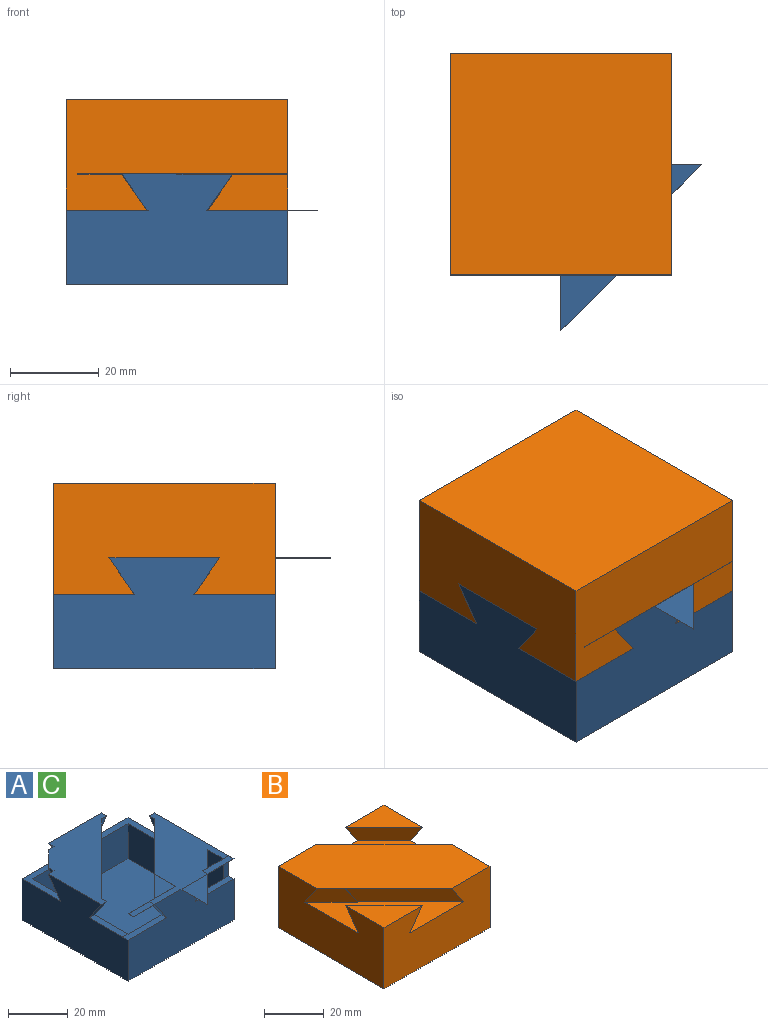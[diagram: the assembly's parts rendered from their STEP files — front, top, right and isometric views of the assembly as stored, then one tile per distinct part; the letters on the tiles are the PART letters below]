
ASSEMBLY  parts=3 mates=1
PART A: 56 faces, bbox 56.8x62.5x25 mm
  f0: plane 50x25mm, normal (-1,0,0), area 997.5mm2, adj f1,f3,f4,f12,f40,f44,f48,f49
  f1: plane 50x25mm, normal (0,1,0), area 997.5mm2, adj f0,f3,f5,f12,f40,f42,f54,f55
  f2: plane 50x47.4mm, normal (0,0,1), area 734.1mm2, adj f4,f5,f6,f7,f13,f18,f21,f25
  f3: plane 37.5x37.5mm, normal (0,0,1), area 624.5mm2, adj f0,f1,f8,f14,f15,f17,f41,f42
  f4: plane 50x25mm, normal (0,-1,0), area 997mm2, adj f0,f2,f5,f12,f30,f31,f32,f35
  f5: plane 50x25mm, normal (1,0,0), area 1101.9mm2, adj f1,f2,f4,f12,f26,f27,f28,f29
  f6: plane 45x22.5mm, normal (0,1,0), area 662.7mm2, adj f2,f13,f15,f16,f19,f23,f24,f25
  f7: plane 7.52x0.03mm, normal (0,1,0), area 0.3mm2, adj f2,f13,f21,f35
  f8: plane 13.05x13.05mm, normal (-0.63,0.63,-0.44), area 131.9mm2, adj f3,f9,f41,f43
  f9: plane 26.75x26.75mm, normal (0,0,-1), area 269.5mm2, adj f8,f14,f15,f17,f41,f42,f43,f44
  f10: plane 13.14x13.14mm, normal (0.63,-0.63,-0.44), area 133mm2, adj f11,f13,f19,f39
  f11: plane 7.42x7.42mm, normal (0,0,1), area 0.3mm2, adj f10,f13,f21,f39
  f12: plane 50x50mm, normal (0,0,-1), area 2500mm2, adj f0,f1,f4,f5
  f13: plane 45x22.5mm, normal (-1,0,0), area 747.3mm2, adj f2,f6,f7,f10,f11,f14,f16,f18
  f14: plane 45x22.5mm, normal (0,-1,0), area 663.5mm2, adj f3,f9,f13,f15,f16,f17,f40,f54
  f15: plane 45x22.5mm, normal (1,0,0), area 663.5mm2, adj f3,f6,f9,f14,f16,f17,f40,f48
  f16: plane 45x45mm, normal (0,0,1), area 2025mm2, adj f6,f13,f14,f15
  f17: plane 32.5x32.5mm, normal (0.63,-0.63,-0.44), area 383.9mm2, adj f3,f9,f14,f15
  f18: plane 28.27x22.52mm, normal (-0.63,0.63,-0.44), area 291.6mm2, adj f2,f13,f22,f23,f25
  f19: plane 26.74x22.5mm, normal (0,0,-1), area 260.6mm2, adj f6,f10,f13,f20,f23,f38,f39
  f20: plane 4.27x0.04mm, normal (0,1,0), area 0.1mm2, adj f13,f19,f22,f23
  f21: plane 7.52x7.52mm, normal (0.63,-0.63,-0.44), area 0.4mm2, adj f2,f7,f11,f13,f35
  f22: plane 4.26x4.26mm, normal (0,0,-1), area 9.1mm2, adj f13,f18,f20
  f23: plane 28.27x22.52mm, normal (-0.63,0.63,-0.44), area 93mm2, adj f6,f18,f19,f20,f24
  f24: plane 9.99x9.98mm, normal (0,0,1), area 49.9mm2, adj f6,f23,f25
  f25: plane 10x0.03mm, normal (-1,0,0), area 0.3mm2, adj f2,f6,f18,f24
  f26: plane 12.51x8.21mm, normal (0.63,-0.63,-0.44), area 0.8mm2, adj f5,f27,f28,f29,f33,f34
  f27: plane 0.03x0.03mm, normal (0,0,1), area 0mm2, adj f5,f26,f34
  f28: plane 6.76x6.76mm, normal (0,0,-1), area 22.9mm2, adj f5,f26,f29
  f29: plane 6.78x0.03mm, normal (0,1,0), area 0.2mm2, adj f5,f26,f28,f33
  f30: plane 12.5x12.5mm, normal (0.63,-0.63,-0.44), area 0.7mm2, adj f2,f4,f31,f32
  f31: plane 12.5x0.03mm, normal (-1,0,0), area 0.4mm2, adj f2,f4,f30,f32
  f32: plane 12.48x12.48mm, normal (0,0,-1), area 77.8mm2, adj f4,f30,f31
  f33: plane 6.78x6.75mm, normal (0,0,1), area 23mm2, adj f5,f26,f29,f34
  f34: plane 8.18x5.73mm, normal (0,0.82,0.57), area 0.3mm2, adj f5,f26,f27,f33
  f35: plane 12.49x2.6mm, normal (0,0,-1), area 31.7mm2, adj f4,f5,f7,f13,f21,f37,f38,f39
  f36: plane 18.24x2.6mm, normal (0,0,1), area 45.8mm2, adj f4,f5,f6,f13,f37,f38
  f37: plane 8.21x2.5mm, normal (0,-1,0), area 20.5mm2, adj f5,f13,f35,f36
  f38: plane 8.21x5.75mm, normal (0.82,0,-0.57), area 26.1mm2, adj f4,f19,f35,f36,f39
  f39: plane 8.35x8.21mm, normal (0,-1,0), area 21.4mm2, adj f10,f11,f19,f35,f38
  f40: plane 18.25x18.25mm, normal (0,0,1), area 85mm2, adj f0,f1,f14,f15,f42,f44
  f41: plane 8.35x8.21mm, normal (0,1,0), area 21.4mm2, adj f3,f8,f9,f42
  f42: plane 8.21x5.75mm, normal (-0.82,0,-0.57), area 26.1mm2, adj f1,f3,f9,f40,f41
  f43: plane 8.35x8.21mm, normal (-1,0,0), area 21.4mm2, adj f3,f8,f9,f44
  f44: plane 8.21x5.75mm, normal (0,0.82,-0.57), area 26.1mm2, adj f0,f3,f9,f40,f43
  f45: plane 2.5x0.03mm, normal (-1,0,0), area 0.1mm2, adj f2,f4,f6,f46
  f46: plane 9.91x2.5mm, normal (0,0,-1), area 24.8mm2, adj f4,f6,f45,f47
  f47: plane 8.21x5.75mm, normal (-0.82,0,-0.57), area 25.1mm2, adj f4,f6,f46,f50
  f48: plane 8.21x5.75mm, normal (0,-0.82,-0.57), area 25.1mm2, adj f0,f3,f15,f49
  f49: plane 18.25x2.5mm, normal (0,0,1), area 39.2mm2, adj f0,f4,f15,f48,f51,f52
  f50: plane 18.25x2.6mm, normal (0,0,1), area 45.9mm2, adj f4,f6,f15,f47,f51,f52
  f51: plane 2.49x0.03mm, normal (0,-1,0), area 0.1mm2, adj f15,f49,f50,f52
  f52: plane 2.6x0.03mm, normal (1,0,0), area 0.1mm2, adj f4,f49,f50,f51
  f53: plane 8.21x5.75mm, normal (0,0.82,-0.57), area 25.1mm2, adj f2,f5,f13,f54
  f54: plane 18.25x18.25mm, normal (0,0,1), area 85mm2, adj f1,f5,f13,f14,f53,f55
  f55: plane 8.21x5.75mm, normal (0.82,0,-0.57), area 25.1mm2, adj f1,f3,f14,f54
PART B: 16 faces, bbox 50x50x25 mm
  f0: plane 50x25mm, normal (0,-1,0), area 1090.5mm2, adj f1,f2,f4,f6,f7,f12,f13,f14
  f1: plane 50x25mm, normal (-1,0,0), area 1092.2mm2, adj f0,f2,f5,f6,f7,f12,f14,f15
  f2: plane 18.03x18.03mm, normal (0,0,1), area 162.6mm2, adj f0,f1,f14
  f3: plane 18.24x18.24mm, normal (0,0,1), area 166.3mm2, adj f4,f5,f9
  f4: plane 50x25mm, normal (1,0,0), area 1092.2mm2, adj f0,f3,f5,f6,f7,f8,f9,f10
  f5: plane 50x25mm, normal (0,1,0), area 1092.2mm2, adj f1,f3,f4,f6,f7,f8,f9,f10
  f6: plane 50x50mm, normal (0,0,1), area 1492.4mm2, adj f0,f1,f4,f5,f10,f11,f13,f15
  f7: plane 50x50mm, normal (0,0,-1), area 2500mm2, adj f0,f1,f4,f5
  f8: plane 37.5x37.5mm, normal (0,0,1), area 625mm2, adj f4,f5,f9,f10
  f9: plane 18.24x18.24mm, normal (-0.63,-0.63,-0.44), area 198.7mm2, adj f3,f4,f5,f8
  f10: plane 37.5x37.5mm, normal (0.63,0.63,-0.44), area 447.7mm2, adj f4,f5,f6,f8
  f11: plane 8.19x5.94mm, normal (0,-1,0), area 1.7mm2, adj f6,f12,f13,f15
  f12: plane 37.5x37.3mm, normal (0,0,1), area 625mm2, adj f0,f1,f11,f13,f14,f15
  f13: plane 30.74x25mm, normal (-0.63,-0.63,-0.44), area 323.2mm2, adj f0,f6,f11,f12
  f14: plane 18.03x18.03mm, normal (0.63,0.63,-0.44), area 196mm2, adj f0,f1,f2,f12
  f15: plane 12.3x12.3mm, normal (-0.63,-0.63,-0.44), area 121.9mm2, adj f1,f6,f11,f12
PART C: same geometry as A
PLACE A at identity
PLACE B rot(axis=(0,1,0),180deg) t=(11.08,0,41.81)mm
PLACE C at identity
MATE cylindrical B.f5 <-> C.f1  axis (0,1,0) through (5.54,26.09,25)mm
